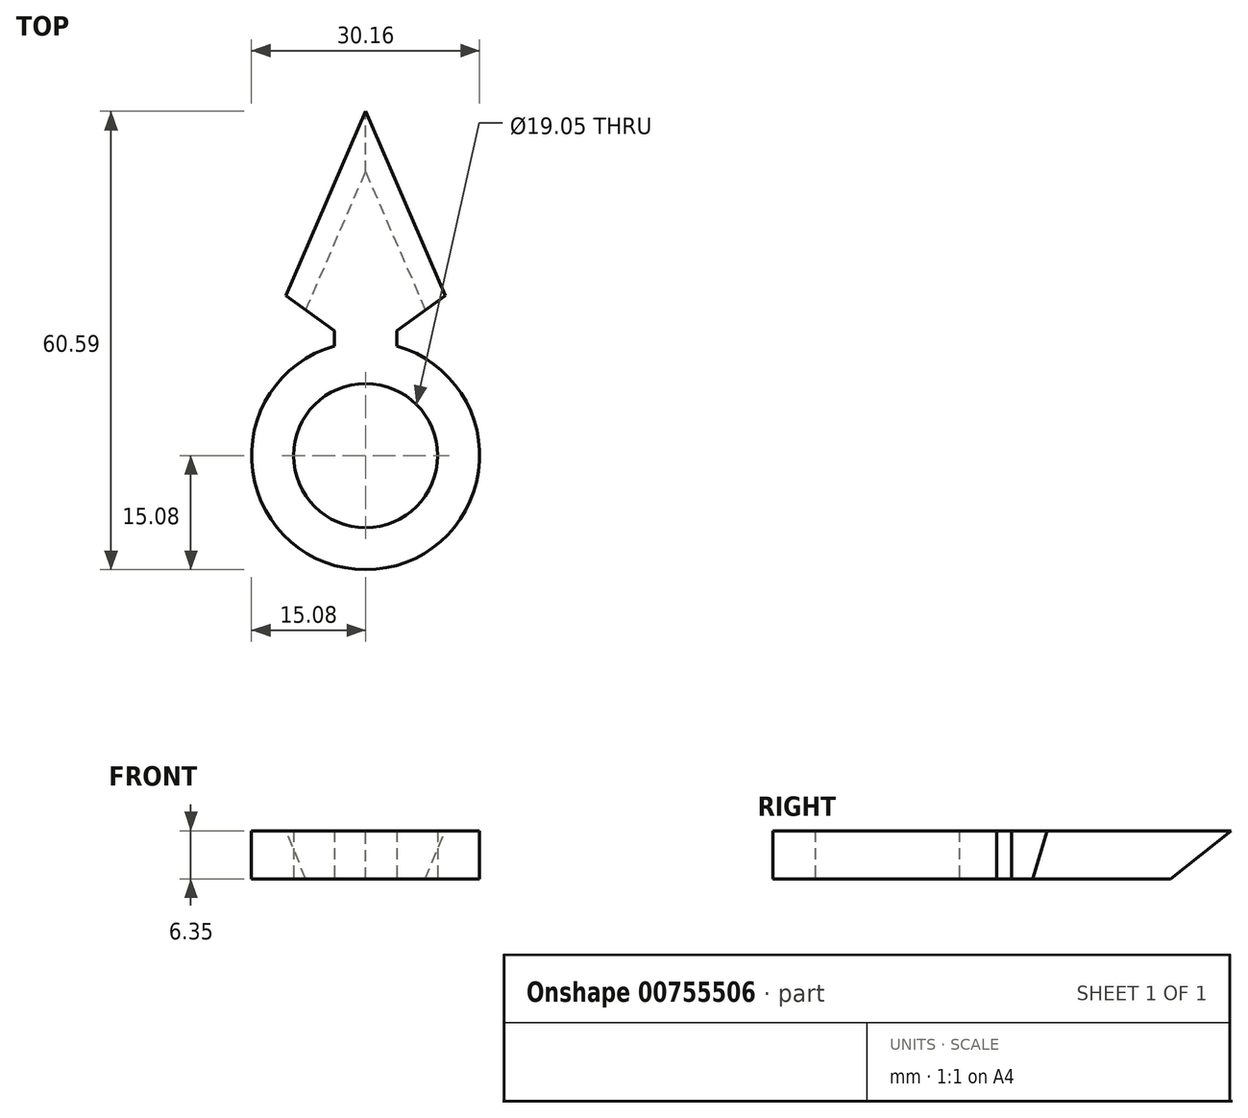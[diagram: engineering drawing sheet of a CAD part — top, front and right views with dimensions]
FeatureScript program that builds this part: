
annotation { "Feature Type Name" : "Feature", "Feature Type Description" : "" }
export const myFeature = defineFeature(function(context is Context, id is Id, definition is map)
    precondition{}
    {
        {
            var Q0;
            Q0=qCreatedBy(makeId("Top.planeOp"),FACE);
            var sketch = newSketch(context, id + "F0", { "sketchPlane" : qUnion([Q0])});
            skCircle(sketch, "E0", {"center": v(0, 0) * mm, "radius": 15.08 * mm});
            skCircle(sketch, "E1", {"center": v(0, 0) * mm, "radius": 9.53 * mm});
            skSolve(sketch);
        }
        {
            var Q0;
            Q0=qSketchRegion(id+"F0",true);
            extrude(context, id + "F1", {"entities" : qUnion([Q0]), "depth" : 6.35 * mm, "offsetDistance" : 25.4 * mm});
        }
        {
            var Q0;
            Q0=qCreatedBy(makeId("Top.planeOp"),FACE);
            var sketch = newSketch(context, id + "F2", { "sketchPlane" : qUnion([Q0])});
            skLineSegment(sketch, "E2", {"start": v(0, 45.5) * mm, "end": v(10.53, 21.15) * mm});
            skLineSegment(sketch, "E3", {"start": v(10.53, 21.15) * mm, "end": v(4.15, 16.5) * mm});
            skLineSegment(sketch, "E4", {"start": v(4.15, 16.5) * mm, "end": v(4.15, 14.5) * mm});
            skArc(sketch, "E5.0", {"start": v(4.15, 14.5) * mm, "mid": v(0, 15.08) * mm, "end": v(-4.15, 14.5) * mm});
            skLineSegment(sketch, "E6", {"start": v(0, 45.5) * mm, "end": v(0, 15.08) * mm, "construction": true});
            skLineSegment(sketch, "E7.MirrorCS", {"start": v(-10.53, 21.15) * mm, "end": v(-4.15, 16.5) * mm});
            skLineSegment(sketch, "E8.MirrorCS", {"start": v(-4.15, 16.5) * mm, "end": v(-4.15, 14.5) * mm});
            skLineSegment(sketch, "E9.MirrorCS", {"start": v(0, 45.5) * mm, "end": v(-10.53, 21.15) * mm});
            skSolve(sketch);
        }
        {
            var Q0;
            Q0=qSketchRegion(id+"F2",true);
            var Q1;
            Q1=makeQuery(id+"F1.opExtrude","CAP_FACE",FACE,{"disambiguationData":[OSD([sQuery(id+"F0.wireOp",EDGE,"E0"),sQuery(id+"F0.wireOp",EDGE,"E1")])],"isStart":false});
            extrude(context, id + "F3", {"entities" : qUnion([Q0]), "operationType" : NewBodyOperationType.ADD, "endBound" : BoundingType.UP_TO_SURFACE, "depth" : 25.4 * mm, "endBoundEntityFace" : qUnion([Q1]), "offsetDistance" : 25.4 * mm});
        }
        {
            var Q0;
            Q0=makeQuery(id+"F3.opExtrude","TWEAK_EDGE",EDGE,{"derivedFrom":[makeQuery(id+"F1.opExtrude","CAP_FACE",FACE,{"disambiguationData":[OSD([sQuery(id+"F0.wireOp",EDGE,"E0"),sQuery(id+"F0.wireOp",EDGE,"E1")])],"isStart":false}),makeQuery(id+"F2.imprint","IMPRINT",EDGE,{"derivedFrom":sQuery(id+"F2.wireOp",EDGE,"E9.MirrorCS")})]});
            var Q1;
            Q1=makeQuery(id+"F3.opExtrude","CAP_EDGE",EDGE,{"disambiguationData":[OSD([sQuery(id+"F2.wireOp",EDGE,"E9.MirrorCS")])],"isStart":true});
            var Q2;
            Q2=makeQuery(id+"F3.opExtrude","TWEAK_EDGE",EDGE,{"derivedFrom":[makeQuery(id+"F1.opExtrude","CAP_FACE",FACE,{"disambiguationData":[OSD([sQuery(id+"F0.wireOp",EDGE,"E0"),sQuery(id+"F0.wireOp",EDGE,"E1")])],"isStart":false}),makeQuery(id+"F2.imprint","IMPRINT",EDGE,{"derivedFrom":sQuery(id+"F2.wireOp",EDGE,"E2")})]});
            var Q3;
            Q3=makeQuery(id+"F3.opExtrude","CAP_EDGE",EDGE,{"disambiguationData":[OSD([sQuery(id+"F2.wireOp",EDGE,"E2")])],"isStart":true});
            chamfer(context, id + "F4", {"entities" : qUnion([Q0, Q1, Q2, Q3]), "chamferType" : ChamferType.TWO_OFFSETS, "width1" : 3.17 * mm, "oppositeDirection" : true, "width2" : 6.35 * mm, "tangentPropagation" : true});
        }
        {
            var Q0;
            Q0=qCreatedBy(makeId("Front.planeOp"),FACE);
            var sketch = newSketch(context, id + "F5", { "sketchPlane" : qUnion([Q0])});
            skLineSegment(sketch, "E10", {"start": v(0, 0) * mm, "end": v(0, 40.45) * mm, "construction": true});
            skSolve(sketch);
        }
    });
